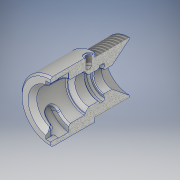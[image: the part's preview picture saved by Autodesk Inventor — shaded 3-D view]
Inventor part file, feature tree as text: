
AUTODESK INVENTOR PART (.ipt)
format: ipt  version: 2019 (Build 230136000, 136)  size: 692,736 bytes
history: native  units: mm
features: other x5, sketch x5, fillet x3, projected_geometry x3, chamfer x2, extrude x2, pattern_circular x1, hole x1
ambient origin geometry x8: Origin, YZ Plane, XZ Plane, XY Plane, X Axis, Y Axis, Z Axis, Center Point
bodies: Solide1 (feature_tree)
feature tree (22):
  other  "Révolution1"
  other  "Filetage1"
  fillet  "Congé1"  Radius=22.0mm
  chamfer  "Chanfrein1"  Distance=3.0mm
  extrude  "Extrusion1"  Depth=2.0mm
  other  "Hélicoïde1"
  fillet  "Congé2"  Radius=16.0mm
  fillet  "Congé3"  Radius=2.0mm
  chamfer  "Chanfrein3"  Distance=2.0mm
  pattern_circular  "Réseau circulaire3"  Count=2  [1 undecoded]
  other  "Plan de construction3"
  extrude  "Extrusion4"  Depth=3.0mm
  hole  "Perçage3"  [1 undecoded]
  sketch  "Esquisse1"
  sketch  "Esquisse3"
  projected_geometry  "Boucle projetée1"
  projected_geometry  "Boucle projetée2"
  sketch  "Esquisse4"
  sketch  "Esquisse9"
  sketch  "Esquisse10"
  projected_geometry  "Boucle projetée3"
  other  "Projeter les arêtes coupées1"
note: 2 required parameter values undecoded (feature->parameter linkage not recoverable at this tier; creation-order binding heuristic only, values carry confidence <= 0.55)
